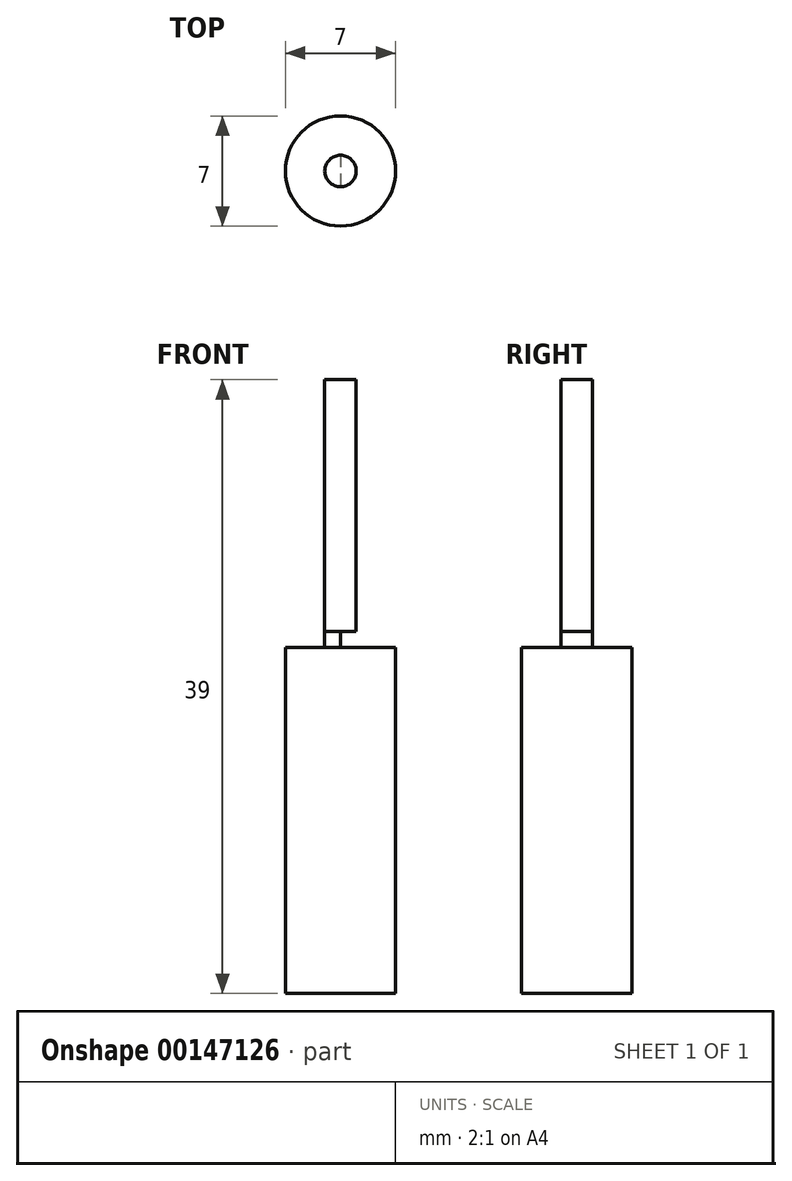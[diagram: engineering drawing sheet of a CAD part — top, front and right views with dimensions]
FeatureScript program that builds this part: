
annotation { "Feature Type Name" : "Feature", "Feature Type Description" : "" }
export const myFeature = defineFeature(function(context is Context, id is Id, definition is map)
    precondition{}
    {
        {
            var Q0;
            Q0=qCreatedBy(makeId("Top.planeOp"),FACE);
            var sketch = newSketch(context, id + "F0", { "sketchPlane" : qUnion([Q0])});
            skPoint(sketch, "E0.middle", {"position": v(0, 0) * mm});
            skCircle(sketch, "E1", {"center": v(0, 0) * mm, "radius": 1 * mm});
            skCircle(sketch, "E2", {"center": v(0, 0) * mm, "radius": 3.5 * mm});
            skLineSegment(sketch, "E3", {"start": v(0, 0) * mm, "end": v(0, -1) * mm});
            skLineSegment(sketch, "E4", {"start": v(0, -1) * mm, "end": v(0, 1) * mm});
            skSolve(sketch);
        }
        {
            var Q0;
            Q0=qSketchRegion(id+"F0",true);
            var Q1;
            Q1=makeQuery(id+"F0.imprint","IMPRINT",FACE,{"disambiguationData":[TD([[makeQuery(id+"F0.imprint","IMPRINT",EDGE,{"derivedFrom":sQuery(id+"F0.wireOp",EDGE,"uYGc6gbQ-b4I5-IUv8-2ImV-eN4ShZYCs7Or.bottom")}),1.0]])]});
            var Q2;
            Q2=makeQuery(id+"F0.imprint","IMPRINT",FACE,{"disambiguationData":[TD([[makeQuery(id+"F0.imprint","IMPRINT",EDGE,{"derivedFrom":sQuery(id+"F0.wireOp",EDGE,"E1")}),1.0]])]});
            extrude(context, id + "F1", {"entities" : qUnion([Q0, Q1, Q2]), "oppositeDirection" : true, "depth" : 22 * mm});
        }
        {
            var Q0;
            Q0=makeQuery(id+"F0.imprint","IMPRINT",FACE,{"disambiguationData":[TD([[makeQuery(id+"F0.imprint","IMPRINT",EDGE,{"derivedFrom":sQuery(id+"F0.wireOp",EDGE,"E1")}),1.0]])]});
            extrude(context, id + "F2", {"entities" : qUnion([Q0]), "operationType" : NewBodyOperationType.ADD, "depth" : 17 * mm, "hasSecondDirection" : true, "secondDirectionOppositeDirection" : false, "secondDirectionDepth" : 1 * mm});
        }
        {
            var Q0;
            {var subQ0=sQuery(id+"F0.wireOp",EDGE,"E4");var subQ4=makeQuery(id+"F0.imprint","IMPRINT",VERTEX,{"derivedFrom":subQ0});Q0=makeQuery(id+"F0.imprint","IMPRINT",FACE,{"disambiguationData":[TD([[makeQuery(id+"F0.imprint","IMPRINT",EDGE,{"disambiguationData":[TD([[subQ4,1.0]])],"derivedFrom":subQ0}),1.0]])]});}
            extrude(context, id + "F3", {"entities" : qUnion([Q0]), "depth" : 1 * mm});
        }
    });
